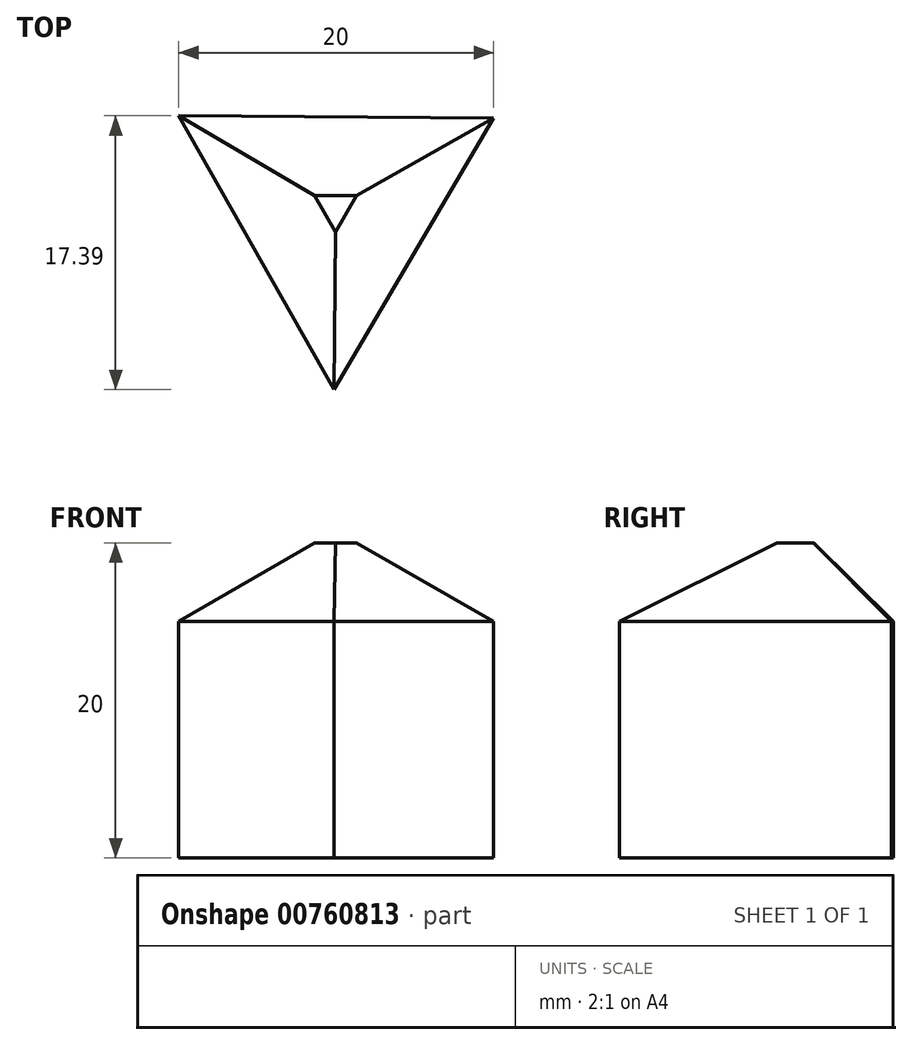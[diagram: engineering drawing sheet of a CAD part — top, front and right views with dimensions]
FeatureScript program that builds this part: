
annotation { "Feature Type Name" : "Feature", "Feature Type Description" : "" }
export const myFeature = defineFeature(function(context is Context, id is Id, definition is map)
    precondition{}
    {
        {
            var Q0;
            Q0=qCreatedBy(makeId("Top.planeOp"),FACE);
            var sketch = newSketch(context, id + "F0", { "sketchPlane" : qUnion([Q0])});
            skCircle(sketch, "E0.cCircle", {"center": v(-24.98, 15.53) * mm, "radius": 5.77 * mm, "construction": true});
            skLineSegment(sketch, "E0.0", {"start": v(-14.94, 21.24) * mm, "end": v(-25.07, 3.99) * mm});
            skLineSegment(sketch, "E0.1", {"start": v(-25.07, 3.99) * mm, "end": v(-34.94, 21.38) * mm});
            skLineSegment(sketch, "E0.2", {"start": v(-34.94, 21.38) * mm, "end": v(-14.94, 21.24) * mm});
            skPoint(sketch, "E0.0.midPoint", {"position": v(-20, 12.61) * mm});
            skSolve(sketch);
        }
        {
            var Q0;
            Q0=makeQuery(id+"F0.imprint","IMPRINT",FACE,{"disambiguationData":[TD([[makeQuery(id+"F0.imprint","IMPRINT",EDGE,{"derivedFrom":sQuery(id+"F0.wireOp",EDGE,"E0.0")}),-1.0]])]});
            extrude(context, id + "F1", {"entities" : qUnion([Q0]), "depth" : 20 * mm, "offsetDistance" : 25 * mm});
        }
        {
            var Q0;
            Q0=makeQuery(id+"F1.opExtrude","CAP_FACE",FACE,{"disambiguationData":[OSD([sQuery(id+"F0.wireOp",EDGE,"E0.0"),sQuery(id+"F0.wireOp",EDGE,"E0.1"),sQuery(id+"F0.wireOp",EDGE,"E0.2")])],"isStart":false});
            chamfer(context, id + "F2", {"entities" : qUnion([Q0]), "width" : 5 * mm, "tangentPropagation" : true});
        }
    });
